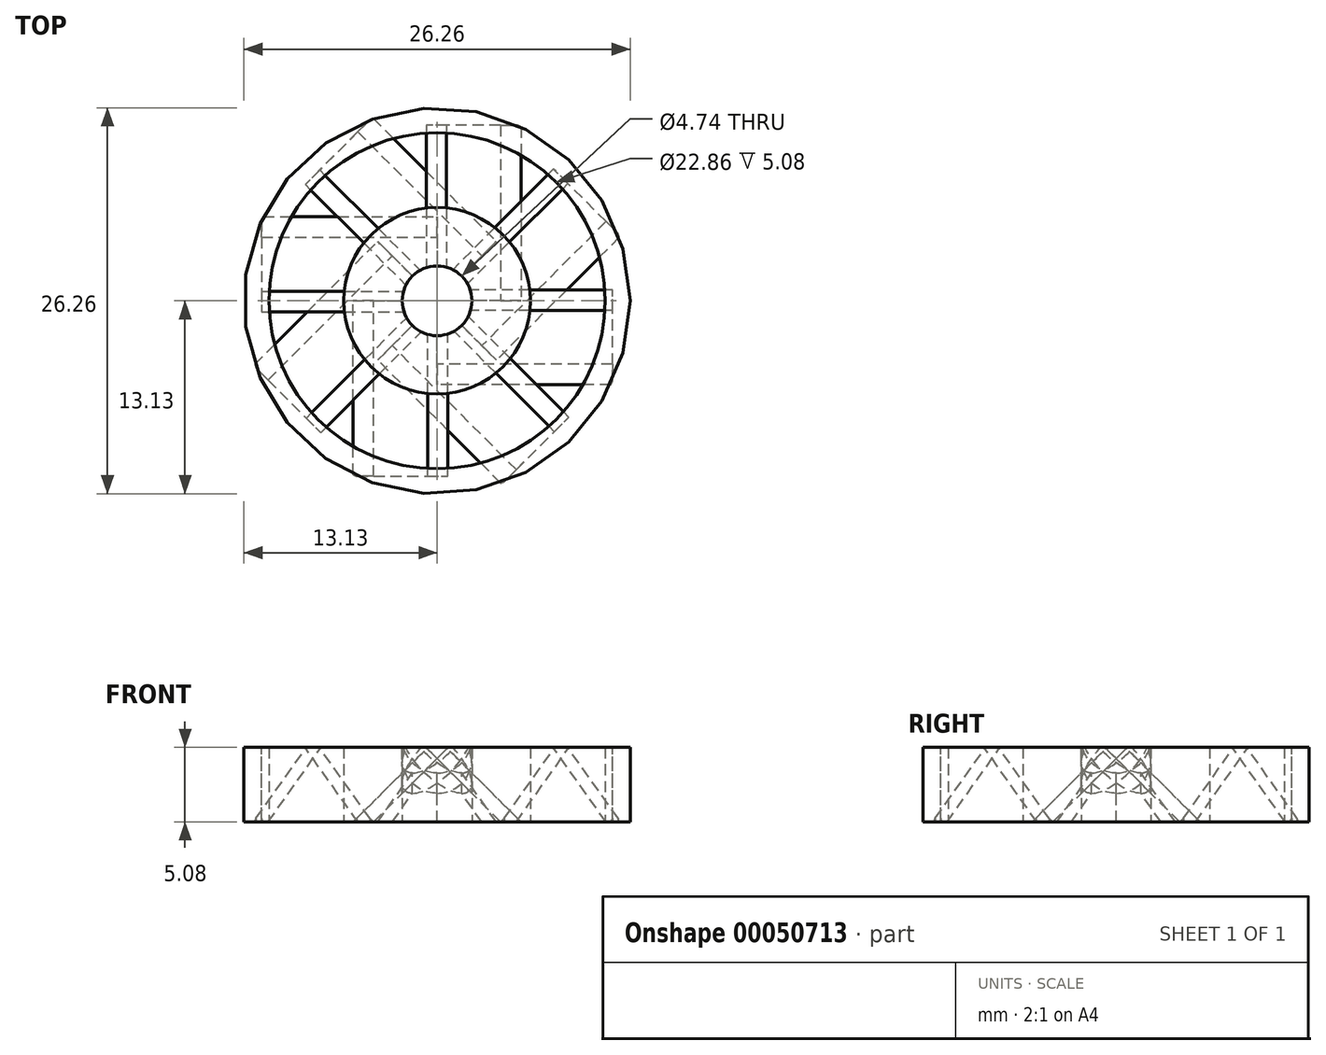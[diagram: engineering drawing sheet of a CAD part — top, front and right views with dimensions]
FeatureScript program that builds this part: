
annotation { "Feature Type Name" : "Feature", "Feature Type Description" : "" }
export const myFeature = defineFeature(function(context is Context, id is Id, definition is map)
    precondition{}
    {
        {
            var Q0;
            Q0=qCreatedBy(makeId("Top.planeOp"),FACE);
            var sketch = newSketch(context, id + "F0", { "sketchPlane" : qUnion([Q0])});
            skCircle(sketch, "E0", {"center": v(0, 0) * mm, "radius": 2.37 * mm});
            skCircle(sketch, "E1", {"center": v(0, 0) * mm, "radius": 13.13 * mm});
            skCircle(sketch, "E2", {"center": v(0, 0) * mm, "radius": 11.43 * mm});
            skCircle(sketch, "E3", {"center": v(0, 0) * mm, "radius": 6.35 * mm});
            skSolve(sketch);
        }
        {
            var Q0;
            Q0 = qSketchRegion(id + "F0", true);
            var Q1;
            Q1=makeQuery(id+"F0.imprint","IMPRINT",FACE,{"disambiguationData":[TD([[makeQuery(id+"F0.imprint","IMPRINT",EDGE,{"derivedFrom":sQuery(id+"F0.wireOp",EDGE,"E0")}),-1.0]])]});
            extrude(context, id + "F1", {"entities" : qUnion([Q0, Q1]), "depth" : 5.08 * mm});
        }
        {
            var Q0;
            Q0=qCreatedBy(makeId("Front.planeOp"),FACE);
            var sketch = newSketch(context, id + "F2", { "sketchPlane" : qUnion([Q0])});
            skPoint(sketch, "E4.orphan", {"position": v(4.58, 0) * mm});
            skLineSegment(sketch, "E5", {"start": v(4.32, 0) * mm, "end": v(-0.74, 5.05) * mm});
            skLineSegment(sketch, "E6", {"start": v(4.32, 0) * mm, "end": v(5.7, 0) * mm});
            skLineSegment(sketch, "E7", {"start": v(5.7, 0) * mm, "end": v(0.65, 5.05) * mm});
            skLineSegment(sketch, "E8", {"start": v(0.65, 5.05) * mm, "end": v(-0.74, 5.05) * mm});
            skSolve(sketch);
        }
        {
            var Q0;
            Q0 = qSketchRegion(id + "F2", true);
            extrude(context, id + "F3", {"entities" : qUnion([Q0]), "oppositeDirection" : true, "depth" : 11.94 * mm});
        }
        {
            var Q0;
            Q0=makeQuery(id+"F1.opExtrude","CAP_FACE",FACE,{"disambiguationData":[OSD([sQuery(id+"F0.wireOp",EDGE,"E0"),sQuery(id+"F0.wireOp",EDGE,"E3")])],"isStart":false});
            var sketch = newSketch(context, id + "F4", { "sketchPlane" : qUnion([Q0])});
            skSolve(sketch);
        }
        {
            var Q0;
            Q0=makeQuery(id+"F4.imprint","IMPRINT",FACE,{"disambiguationData":[TD([[makeQuery(id+"F4.imprint","IMPRINT",EDGE,{"derivedFrom":makeQuery(id+"F1.opExtrude","CAP_EDGE",EDGE,{"disambiguationData":[OSD([sQuery(id+"F0.wireOp",EDGE,"E0")])],"isStart":false})}),1.0]])]});
            extrude(context, id + "F5", {"entities" : qUnion([Q0]), "operationType" : NewBodyOperationType.REMOVE, "endBound" : BoundingType.SYMMETRIC, "oppositeDirection" : true, "depth" : 25.4 * mm});
        }
        {
            var Q0;
            Q0=makeQuery(id+"F1.opExtrude","CAP_FACE",FACE,{"disambiguationData":[OSD([sQuery(id+"F0.wireOp",EDGE,"E1"),sQuery(id+"F0.wireOp",EDGE,"E2")])],"isStart":true});
            var sketch = newSketch(context, id + "F6", { "sketchPlane" : qUnion([Q0])});
            skCircle(sketch, "E9", {"center": v(0, 0) * mm, "radius": 14.68 * mm});
            skCircle(sketch, "E10", {"center": v(0, 0) * mm, "radius": 13.13 * mm});
            skSolve(sketch);
        }
        {
            var Q0;
            Q0 = qSketchRegion(id + "F6", true);
            extrude(context, id + "F7", {"entities" : qUnion([Q0]), "operationType" : NewBodyOperationType.REMOVE, "endBound" : BoundingType.SYMMETRIC, "oppositeDirection" : true, "depth" : 25.4 * mm});
        }
        {
            var Q0;
            Q0=makeQuery(id+"F3.opExtrude","SWEPT_BODY",BODY,{"disambiguationData":[OSD([sQuery(id+"F2.wireOp",EDGE,"Z6NoPrNF-UA8X-9S28-Ei4f-S2LKOp9hV2dw"),sQuery(id+"F2.wireOp",EDGE,"fzxjuVVz-MSKK-uqR1-bF7y-DoyGHMq0184m"),sQuery(id+"F2.wireOp",EDGE,"10EozIW3-OjiH-lRYq-la9H-BkqV8zFRLcrb"),sQuery(id+"F2.wireOp",EDGE,"rsihbXTM-JW3a-qi23-0xbu-VMoOqvGgsLdQ")])]});
            var Q1;
            Q1=makeQuery(id+"F3.opExtrude","SWEPT_BODY",BODY,{"disambiguationData":[OSD([sQuery(id+"F2.wireOp",EDGE,"E5"),sQuery(id+"F2.wireOp",EDGE,"dF4YqT63-DW9f-W8Xy-mAgD-BUfDMrtaRlCM"),sQuery(id+"F2.wireOp",EDGE,"ZY60nGAT-ljQa-54yB-J9gG-ssmvZq1qScGh"),sQuery(id+"F2.wireOp",EDGE,"eSlxrTVd-eFtM-C0Ig-ssm5-R0hhzCxg2ZcJ")])]});
            var Q2;
            Q2=makeQuery(id+"F1.opExtrude","CAP_EDGE",EDGE,{"disambiguationData":[OSD([sQuery(id+"F0.wireOp",EDGE,"E0")])],"isStart":false});
            circularPattern(context, id + "F8", {"entities" : qUnion([Q0, Q1]), "axis" : qUnion([Q2]), "angle" : 45 * degree, "instanceCount" : 8});
        }
    });
